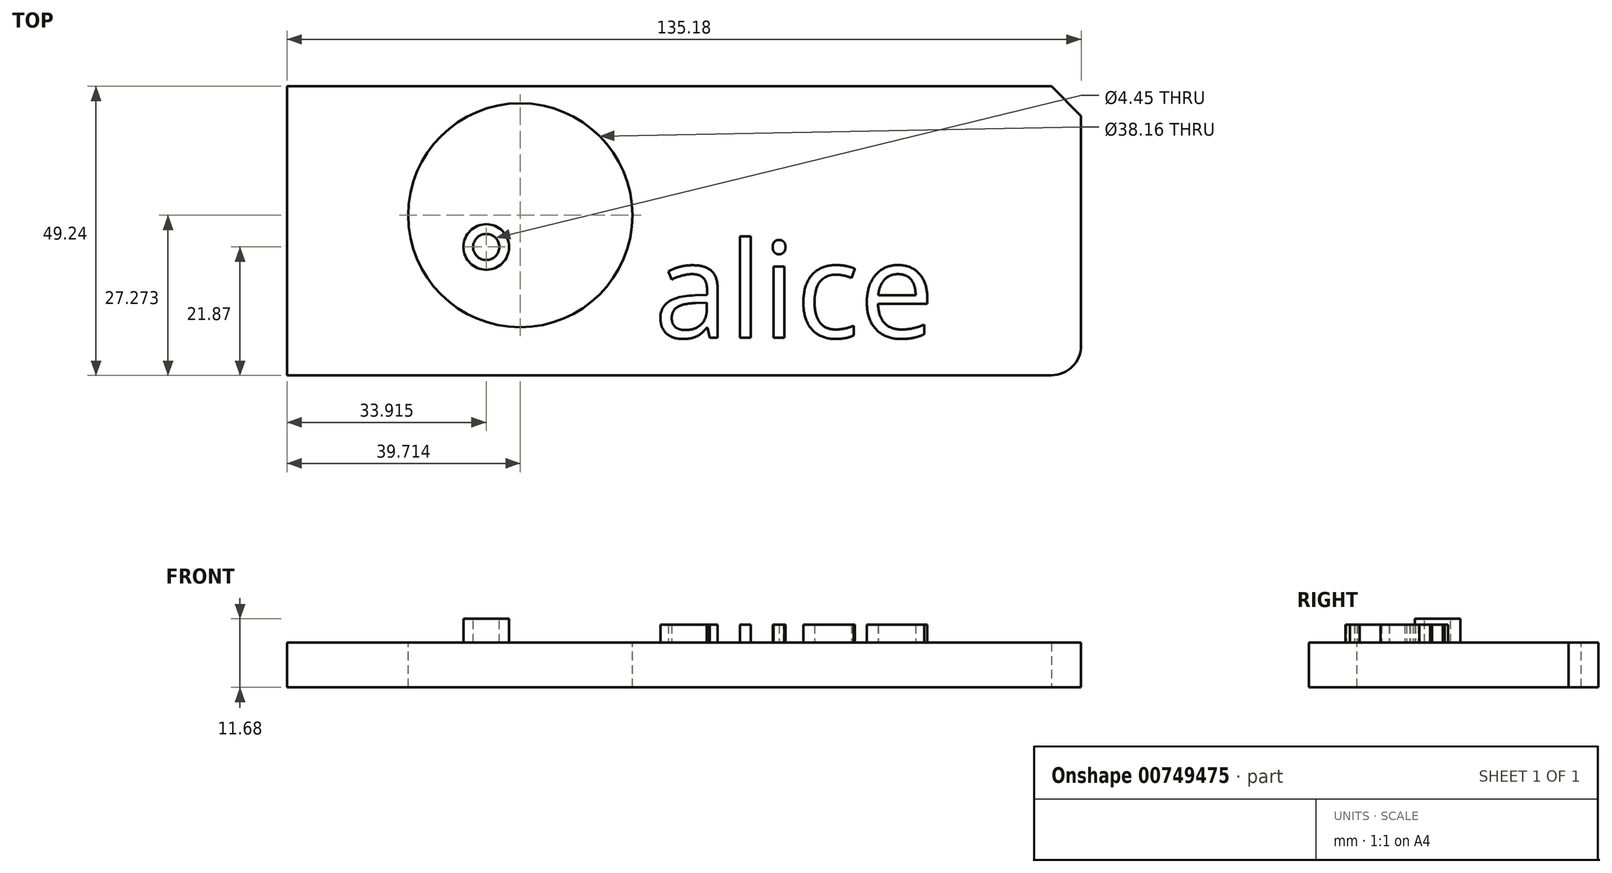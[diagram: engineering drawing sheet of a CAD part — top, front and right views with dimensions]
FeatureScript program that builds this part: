
annotation { "Feature Type Name" : "Feature", "Feature Type Description" : "" }
export const myFeature = defineFeature(function(context is Context, id is Id, definition is map)
    precondition{}
    {
        {
            var Q0;
            Q0=qCreatedBy(makeId("Top.planeOp"),FACE);
            var sketch = newSketch(context, id + "F0", { "sketchPlane" : qUnion([Q0])});
            skLineSegment(sketch, "E0.bottom", {"start": v(-67.84, 35.12) * mm, "end": v(67.34, 35.12) * mm});
            skLineSegment(sketch, "E0.top", {"start": v(-67.84, -14.12) * mm, "end": v(67.34, -14.12) * mm});
            skLineSegment(sketch, "E0.left", {"start": v(-67.84, 35.12) * mm, "end": v(-67.84, -14.12) * mm});
            skLineSegment(sketch, "E0.right", {"start": v(67.34, 35.12) * mm, "end": v(67.34, -14.12) * mm});
            skSolve(sketch);
        }
        {
            var Q0;
            Q0 = qSketchRegion(id + "F0", true);
            extrude(context, id + "F1", {"entities" : qUnion([Q0]), "depth" : 7.62 * mm, "offsetDistance" : 25.4 * mm});
        }
        {
            var Q0;
            Q0=makeQuery(id+"F1.opExtrude","CAP_FACE",FACE,{"disambiguationData":[OSD([sQuery(id+"F0.wireOp",EDGE,"E0.bottom"),sQuery(id+"F0.wireOp",EDGE,"E0.top"),sQuery(id+"F0.wireOp",EDGE,"E0.left"),sQuery(id+"F0.wireOp",EDGE,"E0.right")])],"isStart":false});
            var sketch = newSketch(context, id + "F2", { "sketchPlane" : qUnion([Q0])});
            skCircle(sketch, "E1", {"center": v(-28.13, 13.15) * mm, "radius": 19.08 * mm});
            skSolve(sketch);
        }
        {
            var Q0;
            Q0=makeQuery(id+"F2.imprint","IMPRINT",FACE,{"disambiguationData":[TD([[makeQuery(id+"F2.imprint","IMPRINT",EDGE,{"derivedFrom":sQuery(id+"F2.wireOp",EDGE,"E1")}),1.0]])]});
            extrude(context, id + "F3", {"entities" : qUnion([Q0]), "operationType" : NewBodyOperationType.REMOVE, "oppositeDirection" : true, "depth" : 25.4 * mm, "offsetDistance" : 25.4 * mm});
        }
        {
            var Q0;
            Q0=makeQuery(id+"F1.opExtrude","SWEPT_EDGE",EDGE,{"disambiguationData":[OSD([sQuery(id+"F0.wireOp",EDGE,"E0.top"),sQuery(id+"F0.wireOp",EDGE,"E0.right")])]});
            fillet(context, id + "F4", {"entities" : qUnion([Q0]), "radius" : 5.08 * mm, "tangentPropagation" : true, "allowEdgeOverflow" : false});
        }
        {
            var Q0;
            Q0=makeQuery(id+"F1.opExtrude","SWEPT_EDGE",EDGE,{"disambiguationData":[OSD([sQuery(id+"F0.wireOp",EDGE,"E0.bottom"),sQuery(id+"F0.wireOp",EDGE,"E0.right")])]});
            chamfer(context, id + "F5", {"entities" : qUnion([Q0]), "width" : 5.08 * mm, "tangentPropagation" : true});
        }
        {
            var Q0;
            Q0=makeQuery(id+"F1.opExtrude","CAP_FACE",FACE,{"disambiguationData":[OSD([sQuery(id+"F0.wireOp",EDGE,"E0.bottom"),sQuery(id+"F0.wireOp",EDGE,"E0.top"),sQuery(id+"F0.wireOp",EDGE,"E0.left"),sQuery(id+"F0.wireOp",EDGE,"E0.right")])],"isStart":false});
            var sketch = newSketch(context, id + "F6", { "sketchPlane" : qUnion([Q0])});
            skText(sketch, "E2", { "text": "alice", "fontName": "OpenSans-Regular.ttf"});
            const initialGuessF6  = {"E2": [-0.00532, -0.0077, 1, 0, 0.01634]};
            skSetInitialGuess(sketch, initialGuessF6);
            skSolve(sketch);
        }
        {
            var Q0;
            Q0 = qSketchRegion(id + "F6", true);
            extrude(context, id + "F7", {"entities" : qUnion([Q0]), "operationType" : NewBodyOperationType.ADD, "depth" : 3.05 * mm, "offsetDistance" : 25.4 * mm});
        }
        {
            var Q0;
            {var subQ0=sQuery(id+"F0.wireOp",EDGE,"E0.right");var subQ1=sQuery(id+"F0.wireOp",EDGE,"E0.top");var subQ2=sQuery(id+"F0.wireOp",EDGE,"E0.bottom");var subQ3=sQuery(id+"F0.wireOp",EDGE,"E0.left");Q0=makeQuery(id+"F7.boolean.opBoolean","SPLIT",FACE,{"disambiguationData":[TD([makeQuery(id+"F1.opExtrude","SWEPT_FACE",FACE,{"disambiguationData":[OSD([subQ2])]})])],"derivedFrom":makeQuery(id+"F1.opExtrude","CAP_FACE",FACE,{"disambiguationData":[OSD([subQ2,subQ1,subQ3,subQ0])],"isStart":false})});}
            var sketch = newSketch(context, id + "F8", { "sketchPlane" : qUnion([Q0])});
            skCircle(sketch, "E3", {"center": v(-33.93, 7.75) * mm, "radius": 3.88 * mm});
            skSolve(sketch);
        }
        {
            var Q0;
            Q0=makeQuery(id+"F8.imprint","IMPRINT",FACE,{"disambiguationData":[TD([[makeQuery(id+"F8.imprint","IMPRINT",EDGE,{"derivedFrom":sQuery(id+"F8.wireOp",EDGE,"E3")}),1.0]])]});
            extrude(context, id + "F9", {"entities" : qUnion([Q0]), "depth" : 4.06 * mm, "offsetDistance" : 25.4 * mm});
        }
        {
            var Q0;
            Q0=makeQuery(id+"F9.opExtrude","CAP_FACE",FACE,{"disambiguationData":[OSD([sQuery(id+"F8.wireOp",EDGE,"E3")])],"isStart":false});
            var sketch = newSketch(context, id + "F10", { "sketchPlane" : qUnion([Q0])});
            skCircle(sketch, "E4", {"center": v(-33.93, 7.75) * mm, "radius": 2.23 * mm});
            skSolve(sketch);
        }
        {
            var Q0;
            Q0=makeQuery(id+"F10.imprint","IMPRINT",FACE,{"disambiguationData":[TD([[makeQuery(id+"F10.imprint","IMPRINT",EDGE,{"derivedFrom":sQuery(id+"F10.wireOp",EDGE,"E4")}),1.0]])]});
            extrude(context, id + "F11", {"entities" : qUnion([Q0]), "operationType" : NewBodyOperationType.REMOVE, "oppositeDirection" : true, "depth" : 25.4 * mm, "offsetDistance" : 25.4 * mm});
        }
    });
